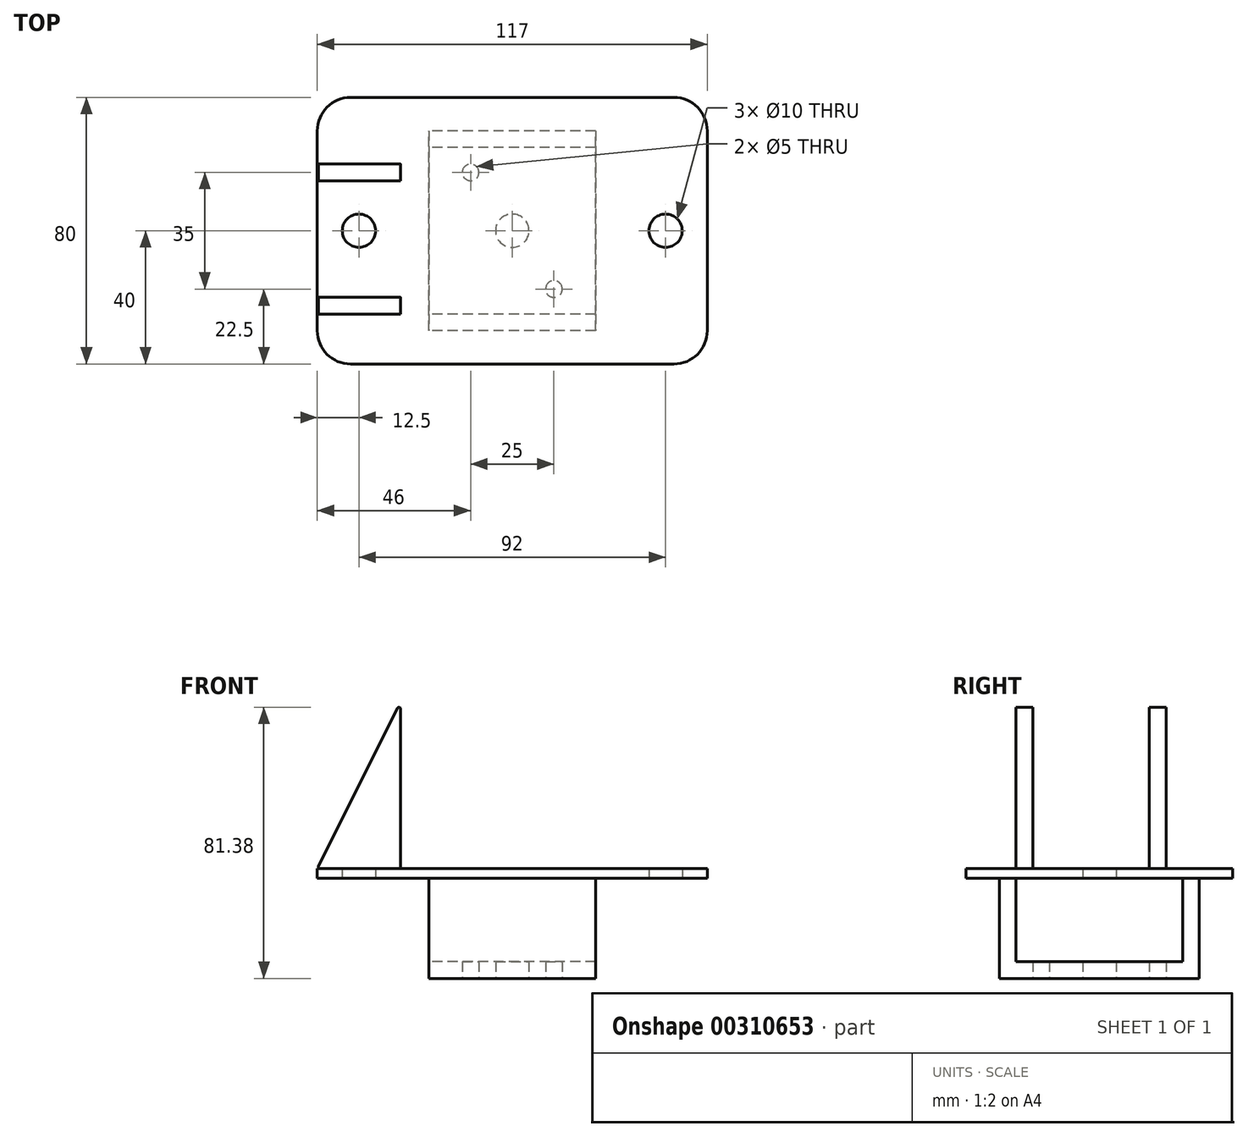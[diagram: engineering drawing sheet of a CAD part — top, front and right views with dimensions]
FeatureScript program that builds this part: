
annotation { "Feature Type Name" : "Feature", "Feature Type Description" : "" }
export const myFeature = defineFeature(function(context is Context, id is Id, definition is map)
    precondition{}
    {
        {
            var Q0;
            Q0=qCreatedBy(makeId("Top.planeOp"),FACE);
            var sketch = newSketch(context, id + "F0", { "sketchPlane" : qUnion([Q0])});
            skLineSegment(sketch, "E0.bottom", {"start": v(10, 0) * mm, "end": v(107, 0) * mm});
            skLineSegment(sketch, "E0.top", {"start": v(10, 80) * mm, "end": v(107, 80) * mm});
            skLineSegment(sketch, "E0.left", {"start": v(0, 10) * mm, "end": v(0, 70) * mm});
            skLineSegment(sketch, "E0.right", {"start": v(117, 10) * mm, "end": v(117, 70) * mm});
            skCircle(sketch, "E1", {"center": v(12.5, 40) * mm, "radius": 5 * mm});
            skCircle(sketch, "E2", {"center": v(104.5, 40) * mm, "radius": 5 * mm});
            skPoint(sketch, "E3", {"position": v(0, 40) * mm});
            skPoint(sketch, "E4.visualSharp", {"position": v(0, 80) * mm});
            skArc(sketch, "E4.filletArc", {"start": v(10, 80) * mm, "mid": v(2.93, 77.07) * mm, "end": v(0, 70) * mm});
            skPoint(sketch, "E5.visualSharp", {"position": v(117, 80) * mm});
            skArc(sketch, "E5.filletArc", {"start": v(117, 70) * mm, "mid": v(114.07, 77.07) * mm, "end": v(107, 80) * mm});
            skPoint(sketch, "E6.visualSharp", {"position": v(117, 0) * mm});
            skArc(sketch, "E6.filletArc", {"start": v(107, 0) * mm, "mid": v(114.07, 2.93) * mm, "end": v(117, 10) * mm});
            skPoint(sketch, "E7.visualSharp", {"position": v(0, 0) * mm});
            skArc(sketch, "E7.filletArc", {"start": v(0, 10) * mm, "mid": v(2.93, 2.93) * mm, "end": v(10, 0) * mm});
            skSolve(sketch);
        }
        {
            var Q0;
            Q0=qSketchRegion(id+"F0",true);
            extrude(context, id + "F1", {"entities" : qUnion([Q0]), "depth" : 3 * mm});
        }
        {
            var Q0;
            Q0=qCreatedBy(makeId("Right.planeOp"),FACE);
            var sketch = newSketch(context, id + "F2", { "sketchPlane" : qUnion([Q0])});
            skLineSegment(sketch, "E8", {"start": v(10, 0) * mm, "end": v(10, -30) * mm});
            skLineSegment(sketch, "E9", {"start": v(10, -30) * mm, "end": v(70, -30) * mm});
            skLineSegment(sketch, "E10", {"start": v(70, -30) * mm, "end": v(70, 0) * mm});
            skLineSegment(sketch, "E11", {"start": v(70, 0) * mm, "end": v(65, 0) * mm});
            skLineSegment(sketch, "E12", {"start": v(65, 0) * mm, "end": v(65, -25) * mm});
            skLineSegment(sketch, "E13", {"start": v(65, -25) * mm, "end": v(15, -25) * mm});
            skLineSegment(sketch, "E14", {"start": v(15, -25) * mm, "end": v(15, 0) * mm});
            skLineSegment(sketch, "E15", {"start": v(15, 0) * mm, "end": v(10, 0) * mm});
            skSolve(sketch);
        }
        {
            var Q0;
            Q0=qSketchRegion(id+"F2",true);
            extrude(context, id + "F3", {"entities" : qUnion([Q0]), "depth" : 50 * mm});
        }
        {
            var Q0;
            Q0=makeQuery(id+"F3.opExtrude","SWEPT_BODY",BODY,{"disambiguationData":[OSD([sQuery(id+"F2.wireOp",EDGE,"E8"),sQuery(id+"F2.wireOp",EDGE,"E9"),sQuery(id+"F2.wireOp",EDGE,"E10"),sQuery(id+"F2.wireOp",EDGE,"E11"),sQuery(id+"F2.wireOp",EDGE,"E12"),sQuery(id+"F2.wireOp",EDGE,"E13"),sQuery(id+"F2.wireOp",EDGE,"E14"),sQuery(id+"F2.wireOp",EDGE,"E15")])]});
            transform(context, id + "F4", {"entities" : qUnion([Q0]), "transformType" : TransformType.TRANSLATION_3D, "dx" : 33.5 * mm, "dy" : 0 * mm, "dz" : 0 * mm, "makeCopy" : false});
        }
        {
            var Q0;
            Q0=makeQuery(id+"F3.opExtrude","SWEPT_FACE",FACE,{"disambiguationData":[OSD([sQuery(id+"F2.wireOp",EDGE,"E9")])]});
            var sketch = newSketch(context, id + "F5", { "sketchPlane" : qUnion([Q0])});
            skCircle(sketch, "E16", {"center": v(58.5, -40) * mm, "radius": 5 * mm});
            skPoint(sketch, "E17", {"position": v(33.5, -40) * mm});
            skPoint(sketch, "E18", {"position": v(58.5, -10) * mm});
            skCircle(sketch, "E19", {"center": v(46, -57.5) * mm, "radius": 2.5 * mm});
            skCircle(sketch, "E20", {"center": v(71, -22.5) * mm, "radius": 2.5 * mm});
            skSolve(sketch);
        }
        {
            var Q0;
            Q0=qSketchRegion(id+"F5",true);
            extrude(context, id + "F6", {"entities" : qUnion([Q0]), "operationType" : NewBodyOperationType.REMOVE, "oppositeDirection" : true, "depth" : 25 * mm});
        }
        {
            var Q0;
            Q0=qCreatedBy(makeId("Front.planeOp"),FACE);
            var sketch = newSketch(context, id + "F7", { "sketchPlane" : qUnion([Q0])});
            skLineSegment(sketch, "E21", {"start": v(25, 50.88) * mm, "end": v(25, 3.5) * mm});
            skLineSegment(sketch, "E22", {"start": v(24.5, 3) * mm, "end": v(0.8, 3) * mm});
            skLineSegment(sketch, "E23", {"start": v(0.36, 3.72) * mm, "end": v(24.05, 51.1) * mm});
            skPoint(sketch, "E24.visualSharp", {"position": v(25, 53) * mm});
            skArc(sketch, "E24.filletArc", {"start": v(25, 50.88) * mm, "mid": v(24.61, 51.37) * mm, "end": v(24.05, 51.1) * mm});
            skPoint(sketch, "E25.visualSharp", {"position": v(0, 3) * mm});
            skArc(sketch, "E25.filletArc", {"start": v(0.36, 3.72) * mm, "mid": v(0.38, 3.24) * mm, "end": v(0.8, 3) * mm});
            skPoint(sketch, "E26.visualSharp", {"position": v(25, 3) * mm});
            skArc(sketch, "E26.filletArc", {"start": v(24.5, 3) * mm, "mid": v(24.85, 3.15) * mm, "end": v(25, 3.5) * mm});
            skSolve(sketch);
        }
        {
            var Q0;
            Q0=qSketchRegion(id+"F7",true);
            extrude(context, id + "F8", {"entities" : qUnion([Q0]), "depth" : 5 * mm});
        }
        {
            var Q0;
            Q0=makeQuery(id+"F8.opExtrude","SWEPT_BODY",BODY,{"disambiguationData":[OSD([sQuery(id+"F7.wireOp",EDGE,"E21"),sQuery(id+"F7.wireOp",EDGE,"E22"),sQuery(id+"F7.wireOp",EDGE,"E23"),sQuery(id+"F7.wireOp",EDGE,"E24.filletArc"),sQuery(id+"F7.wireOp",EDGE,"E25.filletArc"),sQuery(id+"F7.wireOp",EDGE,"E26.filletArc")])]});
            transform(context, id + "F9", {"entities" : qUnion([Q0]), "transformType" : TransformType.TRANSLATION_3D, "dx" : 0 * mm, "dy" : 20 * mm, "dz" : 0 * mm, "makeCopy" : false});
        }
        {
            var Q0;
            Q0=makeQuery(id+"F8.opExtrude","SWEPT_BODY",BODY,{"disambiguationData":[OSD([sQuery(id+"F7.wireOp",EDGE,"E21"),sQuery(id+"F7.wireOp",EDGE,"E22"),sQuery(id+"F7.wireOp",EDGE,"E23"),sQuery(id+"F7.wireOp",EDGE,"E24.filletArc"),sQuery(id+"F7.wireOp",EDGE,"E25.filletArc"),sQuery(id+"F7.wireOp",EDGE,"E26.filletArc")])]});
            transform(context, id + "F10", {"entities" : qUnion([Q0]), "transformType" : TransformType.TRANSLATION_3D, "dx" : 0 * mm, "dy" : 40 * mm, "dz" : 0 * mm, "makeCopy" : true});
        }
    });
